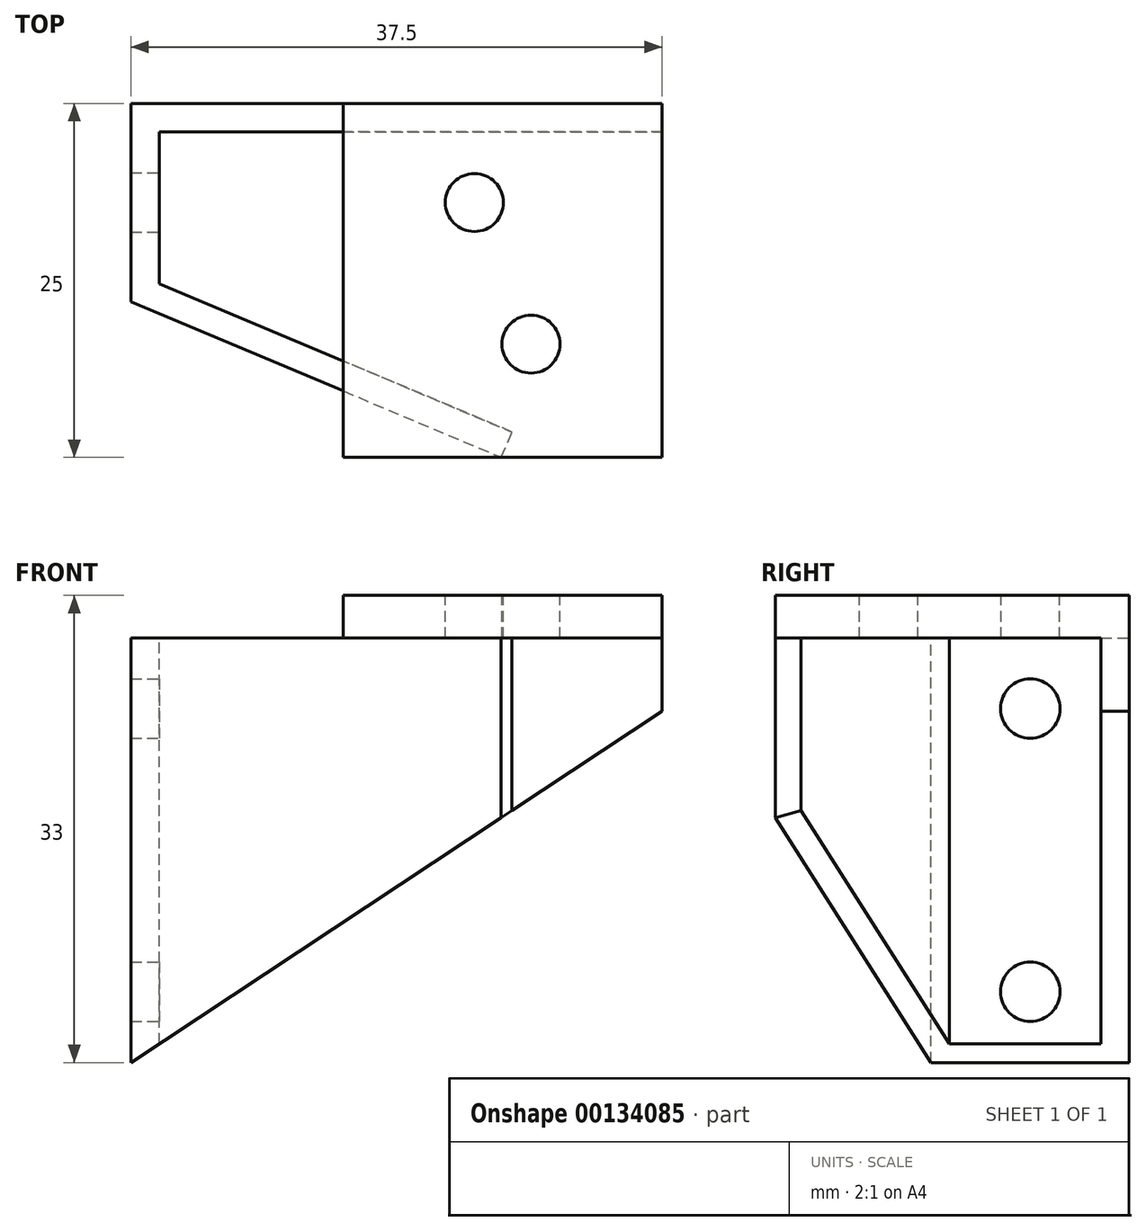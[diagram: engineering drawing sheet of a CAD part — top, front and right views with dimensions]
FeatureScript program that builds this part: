
annotation { "Feature Type Name" : "Feature", "Feature Type Description" : "" }
export const myFeature = defineFeature(function(context is Context, id is Id, definition is map)
    precondition{}
    {
        {
            var Q0;
            Q0=qCreatedBy(makeId("Top.planeOp"),FACE);
            var sketch = newSketch(context, id + "F0", { "sketchPlane" : qUnion([Q0])});
            skLineSegment(sketch, "E0.bottom", {"start": v(0, 0) * mm, "end": v(22.5, 0) * mm});
            skLineSegment(sketch, "E0.top", {"start": v(0, 25) * mm, "end": v(22.5, 25) * mm});
            skLineSegment(sketch, "E0.left", {"start": v(0, 0) * mm, "end": v(0, 25) * mm});
            skLineSegment(sketch, "E0.right", {"start": v(22.5, 0) * mm, "end": v(22.5, 25) * mm});
            skSolve(sketch);
        }
        {
            var Q0;
            Q0 = qSketchRegion(id + "F0", true);
            extrude(context, id + "F1", {"entities" : qUnion([Q0]), "depth" : 3 * mm});
        }
        {
            var Q0;
            Q0=makeQuery(id+"F1.opExtrude","CAP_FACE",FACE,{"disambiguationData":[OSD([sQuery(id+"F0.wireOp",EDGE,"E0.bottom"),sQuery(id+"F0.wireOp",EDGE,"E0.top"),sQuery(id+"F0.wireOp",EDGE,"E0.left"),sQuery(id+"F0.wireOp",EDGE,"E0.right")])],"isStart":false});
            var sketch = newSketch(context, id + "F2", { "sketchPlane" : qUnion([Q0])});
            skCircle(sketch, "E1", {"center": v(9.25, 18) * mm, "radius": 2.05 * mm});
            skCircle(sketch, "E2", {"center": v(13.25, 8) * mm, "radius": 2.05 * mm});
            skLineSegment(sketch, "E3", {"start": v(9.25, 18) * mm, "end": v(9.25, 25) * mm, "construction": true});
            skLineSegment(sketch, "E4", {"start": v(9.25, 18) * mm, "end": v(0, 18) * mm, "construction": true});
            skLineSegment(sketch, "E5.bottom", {"start": v(9.25, 18) * mm, "end": v(13.25, 18) * mm, "construction": true});
            skLineSegment(sketch, "E5.top", {"start": v(9.25, 8) * mm, "end": v(13.25, 8) * mm, "construction": true});
            skLineSegment(sketch, "E5.left", {"start": v(9.25, 18) * mm, "end": v(9.25, 8) * mm, "construction": true});
            skLineSegment(sketch, "E5.right", {"start": v(13.25, 18) * mm, "end": v(13.25, 8) * mm, "construction": true});
            skLineSegment(sketch, "E6", {"start": v(13.25, 18) * mm, "end": v(22.5, 18) * mm, "construction": true});
            skSolve(sketch);
        }
        {
            var Q0;
            Q0 = qSketchRegion(id + "F2", true);
            extrude(context, id + "F3", {"entities" : qUnion([Q0]), "operationType" : NewBodyOperationType.REMOVE, "oppositeDirection" : true, "depth" : 25 * mm});
        }
        {
            var Q0;
            Q0=qCreatedBy(makeId("Top.planeOp"),FACE);
            var sketch = newSketch(context, id + "F4", { "sketchPlane" : qUnion([Q0])});
            skLineSegment(sketch, "E7.bottom", {"start": v(-15, 25) * mm, "end": v(-13, 25) * mm});
            skLineSegment(sketch, "E7.top", {"start": v(-15, 11) * mm, "end": v(-13, 11) * mm});
            skLineSegment(sketch, "E7.left", {"start": v(-15, 25) * mm, "end": v(-15, 11) * mm});
            skLineSegment(sketch, "E7.right", {"start": v(-13, 25) * mm, "end": v(-13, 11) * mm});
            skLineSegment(sketch, "E8", {"start": v(0, 25) * mm, "end": v(-15, 25) * mm, "construction": true});
            skLineSegment(sketch, "E9.bottom", {"start": v(-15, 25) * mm, "end": v(22.5, 25) * mm});
            skLineSegment(sketch, "E9.top", {"start": v(-15, 23) * mm, "end": v(22.5, 23) * mm});
            skLineSegment(sketch, "E9.left", {"start": v(-15, 25) * mm, "end": v(-15, 23) * mm});
            skLineSegment(sketch, "E9.right", {"start": v(22.5, 25) * mm, "end": v(22.5, 23) * mm});
            skLineSegment(sketch, "E10", {"start": v(-15, 11) * mm, "end": v(11.15, 0) * mm});
            skLineSegment(sketch, "E11", {"start": v(11.15, 0) * mm, "end": v(11.9, 1.8) * mm});
            skLineSegment(sketch, "E12", {"start": v(11.9, 1.8) * mm, "end": v(-14.24, 12.8) * mm});
            skLineSegment(sketch, "E13", {"start": v(-14.24, 12.8) * mm, "end": v(-15, 11) * mm});
            skSolve(sketch);
        }
        {
            var Q0;
            Q0 = qSketchRegion(id + "F4", true);
            extrude(context, id + "F5", {"entities" : qUnion([Q0]), "operationType" : NewBodyOperationType.ADD, "oppositeDirection" : true, "depth" : 30 * mm});
        }
        {
            var Q0;
            Q0=qCreatedBy(makeId("Front.planeOp"),FACE);
            var sketch = newSketch(context, id + "F6", { "sketchPlane" : qUnion([Q0])});
            skLineSegment(sketch, "E14", {"start": v(22.5, -5.2) * mm, "end": v(-15, -30) * mm});
            skLineSegment(sketch, "E15", {"start": v(-15, -30) * mm, "end": v(22.5, -30) * mm});
            skLineSegment(sketch, "E16", {"start": v(22.5, -30) * mm, "end": v(22.5, -5.2) * mm});
            skSolve(sketch);
        }
        {
            var Q0;
            Q0 = qSketchRegion(id + "F6", true);
            extrude(context, id + "F7", {"entities" : qUnion([Q0]), "operationType" : NewBodyOperationType.REMOVE, "oppositeDirection" : true, "depth" : 25 * mm});
        }
        {
            var Q0;
            Q0=qCreatedBy(makeId("Right.planeOp"),FACE);
            var sketch = newSketch(context, id + "F8", { "sketchPlane" : qUnion([Q0])});
            skLineSegment(sketch, "E17", {"start": v(18, -30) * mm, "end": v(18, -25) * mm, "construction": true});
            skLineSegment(sketch, "E18", {"start": v(18, -25) * mm, "end": v(18, -5) * mm, "construction": true});
            skLineSegment(sketch, "E19", {"start": v(18, -5) * mm, "end": v(18, 0) * mm, "construction": true});
            skLineSegment(sketch, "E20", {"start": v(25, -13.84) * mm, "end": v(18, -13.84) * mm, "construction": true});
            skLineSegment(sketch, "E21", {"start": v(18, -13.84) * mm, "end": v(11, -13.84) * mm, "construction": true});
            skCircle(sketch, "E22", {"center": v(18, -5) * mm, "radius": 2.1 * mm});
            skCircle(sketch, "E23", {"center": v(18, -25) * mm, "radius": 2.1 * mm});
            skSolve(sketch);
        }
        {
            var Q0;
            Q0 = qSketchRegion(id + "F8", true);
            extrude(context, id + "F9", {"entities" : qUnion([Q0]), "operationType" : NewBodyOperationType.REMOVE, "oppositeDirection" : true, "depth" : 25 * mm});
        }
    });
